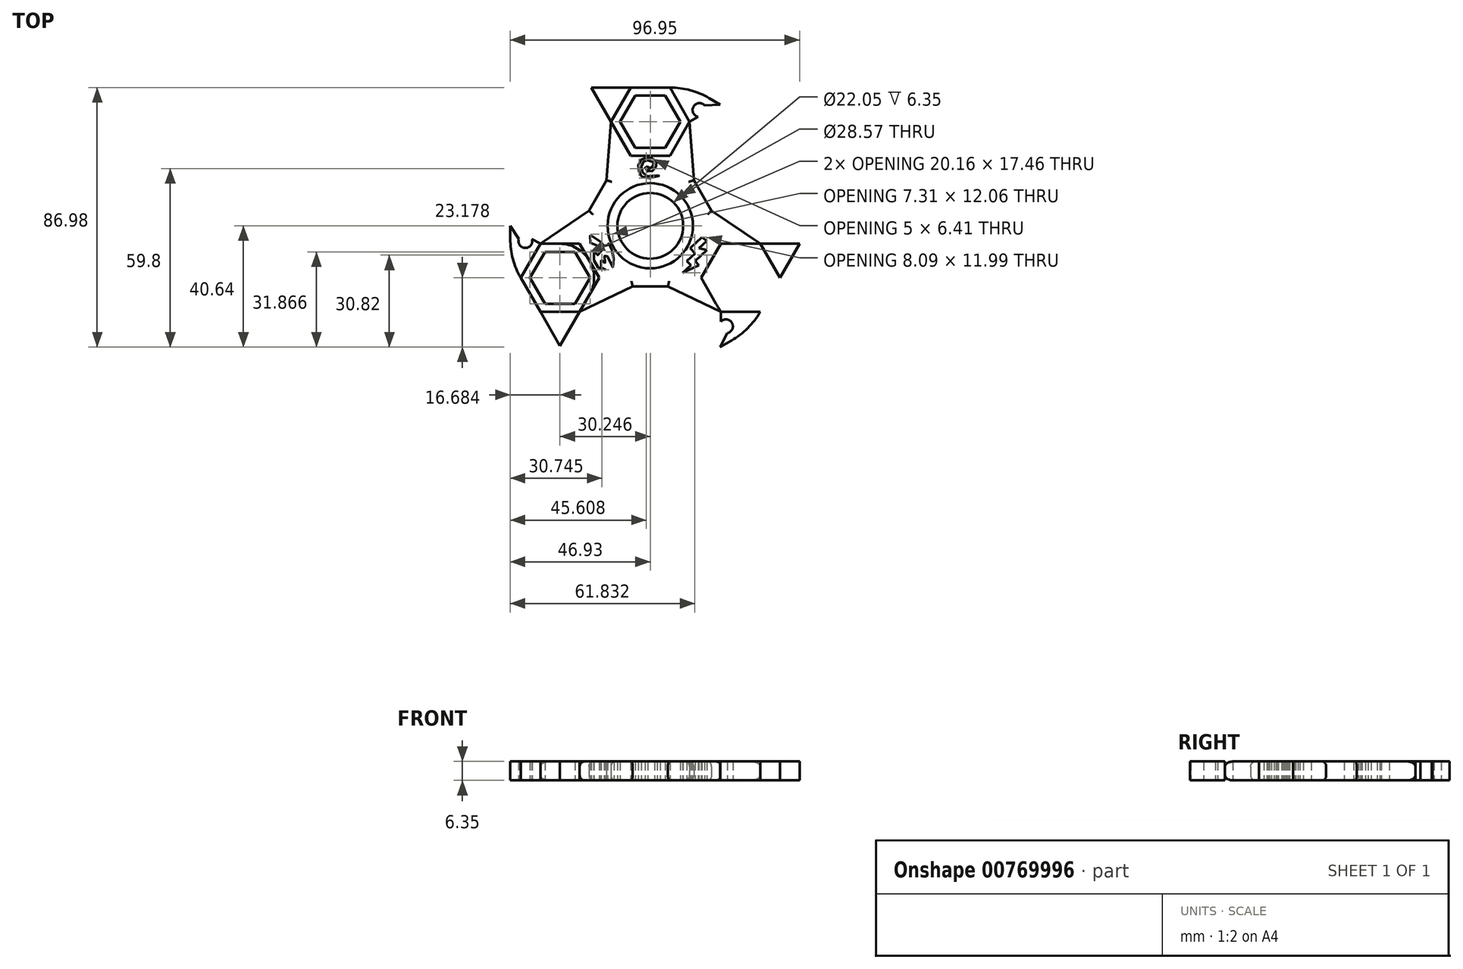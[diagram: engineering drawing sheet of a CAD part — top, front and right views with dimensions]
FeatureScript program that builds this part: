
annotation { "Feature Type Name" : "Feature", "Feature Type Description" : "" }
export const myFeature = defineFeature(function(context is Context, id is Id, definition is map)
    precondition{}
    {
        {
            var Q0;
            Q0=qCreatedBy(makeId("Top.planeOp"),FACE);
            var sketch = newSketch(context, id + "F0", { "sketchPlane" : qUnion([Q0])});
            skCircle(sketch, "E0", {"center": v(0, 0) * mm, "radius": 14.29 * mm});
            skCircle(sketch, "E1", {"center": v(0, 0) * mm, "radius": 11.02 * mm});
            skCircle(sketch, "E2.cCircle", {"center": v(0, 34.93) * mm, "radius": 8.73 * mm, "construction": true});
            skLineSegment(sketch, "E2.0", {"start": v(5.04, 26.2) * mm, "end": v(-5.04, 26.2) * mm});
            skLineSegment(sketch, "E2.1", {"start": v(-5.04, 26.2) * mm, "end": v(-10.08, 34.93) * mm});
            skLineSegment(sketch, "E2.2", {"start": v(-10.08, 34.92) * mm, "end": v(-5.04, 43.66) * mm});
            skLineSegment(sketch, "E2.3", {"start": v(-5.04, 43.66) * mm, "end": v(5.04, 43.66) * mm});
            skLineSegment(sketch, "E2.4", {"start": v(5.04, 43.66) * mm, "end": v(10.08, 34.92) * mm});
            skLineSegment(sketch, "E2.5", {"start": v(10.08, 34.93) * mm, "end": v(5.04, 26.2) * mm});
            skPoint(sketch, "E2.0.midPoint", {"position": v(0, 26.2) * mm});
            skCircle(sketch, "E3.cCircle", {"center": v(0, 34.93) * mm, "radius": 11.42 * mm, "construction": true});
            skLineSegment(sketch, "E3.0", {"start": v(6.6, 23.5) * mm, "end": v(-6.6, 23.5) * mm});
            skLineSegment(sketch, "E3.1", {"start": v(-6.6, 23.5) * mm, "end": v(-13.18, 34.93) * mm});
            skLineSegment(sketch, "E3.2", {"start": v(-13.18, 34.92) * mm, "end": v(-6.6, 46.34) * mm});
            skLineSegment(sketch, "E3.3", {"start": v(-6.6, 46.34) * mm, "end": v(6.6, 46.34) * mm});
            skLineSegment(sketch, "E3.4", {"start": v(6.6, 46.34) * mm, "end": v(13.18, 34.92) * mm});
            skLineSegment(sketch, "E3.5", {"start": v(13.18, 34.92) * mm, "end": v(6.6, 23.5) * mm});
            skPoint(sketch, "E3.0.midPoint", {"position": v(0, 23.5) * mm});
            skPoint(sketch, "E4.center", {"position": v(0.42, -0.28) * mm});
            skCircle(sketch, "E5.1.0", {"center": v(-30.25, -17.46) * mm, "radius": 11.42 * mm, "construction": true});
            skPoint(sketch, "E5.1.1", {"position": v(-20.36, -11.75) * mm});
            skPoint(sketch, "E5.1.2", {"position": v(-22.68, -13.1) * mm});
            skLineSegment(sketch, "E5.1.3", {"start": v(-23.65, -28.88) * mm, "end": v(-36.84, -28.88) * mm});
            skLineSegment(sketch, "E5.1.4", {"start": v(-17.06, -17.46) * mm, "end": v(-23.65, -28.88) * mm});
            skLineSegment(sketch, "E5.1.5", {"start": v(-36.84, -6.05) * mm, "end": v(-23.65, -6.05) * mm});
            skLineSegment(sketch, "E5.1.6", {"start": v(-43.43, -17.46) * mm, "end": v(-36.84, -6.05) * mm});
            skLineSegment(sketch, "E5.1.7", {"start": v(-35.29, -8.73) * mm, "end": v(-25.2, -8.73) * mm});
            skCircle(sketch, "E5.1.8", {"center": v(-30.25, -17.46) * mm, "radius": 8.73 * mm, "construction": true});
            skLineSegment(sketch, "E5.1.9", {"start": v(-40.33, -17.46) * mm, "end": v(-35.29, -8.73) * mm});
            skLineSegment(sketch, "E5.1.10", {"start": v(-20.16, -17.46) * mm, "end": v(-25.2, -26.2) * mm});
            skLineSegment(sketch, "E5.1.11", {"start": v(-35.29, -26.2) * mm, "end": v(-40.33, -17.46) * mm});
            skLineSegment(sketch, "E5.1.12", {"start": v(-25.2, -26.2) * mm, "end": v(-35.29, -26.2) * mm});
            skLineSegment(sketch, "E5.1.13", {"start": v(-36.84, -28.88) * mm, "end": v(-43.43, -17.46) * mm});
            skLineSegment(sketch, "E5.1.14", {"start": v(-23.65, -6.05) * mm, "end": v(-17.06, -17.46) * mm});
            skLineSegment(sketch, "E5.1.15", {"start": v(-25.2, -8.73) * mm, "end": v(-20.16, -17.46) * mm});
            skCircle(sketch, "E5.2.0", {"center": v(30.25, -17.46) * mm, "radius": 11.42 * mm, "construction": true});
            skPoint(sketch, "E5.2.1", {"position": v(20.36, -11.75) * mm});
            skPoint(sketch, "E5.2.2", {"position": v(22.68, -13.1) * mm});
            skLineSegment(sketch, "E5.2.3", {"start": v(36.84, -6.05) * mm, "end": v(43.43, -17.46) * mm});
            skLineSegment(sketch, "E5.2.4", {"start": v(23.65, -6.05) * mm, "end": v(36.84, -6.05) * mm});
            skLineSegment(sketch, "E5.2.5", {"start": v(23.65, -28.88) * mm, "end": v(17.06, -17.46) * mm});
            skLineSegment(sketch, "E5.2.6", {"start": v(36.84, -28.88) * mm, "end": v(23.65, -28.88) * mm});
            skLineSegment(sketch, "E5.2.7", {"start": v(25.2, -26.2) * mm, "end": v(20.16, -17.46) * mm});
            skCircle(sketch, "E5.2.8", {"center": v(30.25, -17.46) * mm, "radius": 8.73 * mm, "construction": true});
            skLineSegment(sketch, "E5.2.9", {"start": v(35.29, -26.2) * mm, "end": v(25.2, -26.2) * mm});
            skLineSegment(sketch, "E5.2.10", {"start": v(25.2, -8.73) * mm, "end": v(35.29, -8.73) * mm});
            skLineSegment(sketch, "E5.2.11", {"start": v(40.33, -17.46) * mm, "end": v(35.29, -26.2) * mm});
            skLineSegment(sketch, "E5.2.12", {"start": v(35.29, -8.73) * mm, "end": v(40.33, -17.46) * mm});
            skLineSegment(sketch, "E5.2.13", {"start": v(43.43, -17.46) * mm, "end": v(36.84, -28.88) * mm});
            skLineSegment(sketch, "E5.2.14", {"start": v(17.06, -17.46) * mm, "end": v(23.65, -6.05) * mm});
            skLineSegment(sketch, "E5.2.15", {"start": v(20.16, -17.46) * mm, "end": v(25.2, -8.73) * mm});
            skSolve(sketch);
        }
        {
            var Q0;
            Q0=qCreatedBy(makeId("Top.planeOp"),FACE);
            var sketch = newSketch(context, id + "F1", { "sketchPlane" : qUnion([Q0])});
            skLineSegment(sketch, "E6.0", {"start": v(-36.84, -6.05) * mm, "end": v(-23.65, -6.05) * mm});
            skCircle(sketch, "E6.1", {"center": v(0, 0) * mm, "radius": 14.29 * mm});
            skLineSegment(sketch, "E6.2", {"start": v(40.33, -17.46) * mm, "end": v(35.29, -26.2) * mm});
            skCircle(sketch, "E6.3", {"center": v(0, 0) * mm, "radius": 11.02 * mm});
            skCircle(sketch, "E6.4", {"center": v(-30.25, -17.46) * mm, "radius": 11.42 * mm});
            skLineSegment(sketch, "E6.5", {"start": v(-10.08, 34.92) * mm, "end": v(-5.04, 43.66) * mm});
            skLineSegment(sketch, "E6.6", {"start": v(-23.65, -28.88) * mm, "end": v(-36.84, -28.88) * mm});
            skLineSegment(sketch, "E6.7", {"start": v(23.65, -28.88) * mm, "end": v(17.06, -17.46) * mm});
            skCircle(sketch, "E6.8", {"center": v(30.25, -17.46) * mm, "radius": 8.73 * mm});
            skLineSegment(sketch, "E6.9", {"start": v(25.2, -26.2) * mm, "end": v(20.16, -17.46) * mm});
            skLineSegment(sketch, "E6.10", {"start": v(-6.6, 46.34) * mm, "end": v(6.6, 46.34) * mm});
            skLineSegment(sketch, "E6.11", {"start": v(-5.04, 26.2) * mm, "end": v(-10.08, 34.93) * mm});
            skLineSegment(sketch, "E6.12", {"start": v(35.29, -26.2) * mm, "end": v(25.2, -26.2) * mm});
            skCircle(sketch, "E6.13", {"center": v(30.25, -17.46) * mm, "radius": 11.42 * mm});
            skLineSegment(sketch, "E6.14", {"start": v(-5.04, 43.66) * mm, "end": v(5.04, 43.66) * mm});
            skLineSegment(sketch, "E6.15", {"start": v(5.04, 43.66) * mm, "end": v(10.08, 34.92) * mm});
            skLineSegment(sketch, "E6.16", {"start": v(-40.33, -17.46) * mm, "end": v(-35.29, -8.73) * mm});
            skLineSegment(sketch, "E6.17", {"start": v(-25.2, -26.2) * mm, "end": v(-35.29, -26.2) * mm});
            skLineSegment(sketch, "E6.18", {"start": v(10.08, 34.93) * mm, "end": v(5.04, 26.2) * mm});
            skLineSegment(sketch, "E6.19", {"start": v(43.43, -17.46) * mm, "end": v(36.84, -28.88) * mm});
            skCircle(sketch, "E6.20", {"center": v(0, 34.93) * mm, "radius": 11.42 * mm});
            skLineSegment(sketch, "E6.21", {"start": v(-35.29, -26.2) * mm, "end": v(-40.33, -17.46) * mm});
            skCircle(sketch, "E6.22", {"center": v(-30.25, -17.46) * mm, "radius": 8.73 * mm});
            skLineSegment(sketch, "E6.23", {"start": v(25.2, -8.73) * mm, "end": v(35.29, -8.73) * mm});
            skLineSegment(sketch, "E6.24", {"start": v(36.84, -6.05) * mm, "end": v(43.43, -17.46) * mm});
            skLineSegment(sketch, "E6.25", {"start": v(-17.06, -17.46) * mm, "end": v(-23.65, -28.88) * mm});
            skLineSegment(sketch, "E6.26", {"start": v(36.84, -28.88) * mm, "end": v(23.65, -28.88) * mm});
            skLineSegment(sketch, "E6.27", {"start": v(-35.29, -8.73) * mm, "end": v(-25.2, -8.73) * mm});
            skLineSegment(sketch, "E6.28", {"start": v(-36.84, -28.88) * mm, "end": v(-43.43, -17.46) * mm});
            skLineSegment(sketch, "E6.29", {"start": v(-13.18, 34.92) * mm, "end": v(-6.6, 46.34) * mm});
            skLineSegment(sketch, "E6.30", {"start": v(-6.6, 23.5) * mm, "end": v(-13.18, 34.93) * mm});
            skLineSegment(sketch, "E6.31", {"start": v(-20.16, -17.46) * mm, "end": v(-25.2, -26.2) * mm});
            skLineSegment(sketch, "E6.32", {"start": v(35.29, -8.73) * mm, "end": v(40.33, -17.46) * mm});
            skLineSegment(sketch, "E6.33", {"start": v(-43.43, -17.46) * mm, "end": v(-36.84, -6.05) * mm});
            skLineSegment(sketch, "E6.34", {"start": v(23.65, -6.05) * mm, "end": v(36.84, -6.05) * mm});
            skLineSegment(sketch, "E6.35", {"start": v(6.6, 46.34) * mm, "end": v(13.18, 34.92) * mm});
            skLineSegment(sketch, "E6.36", {"start": v(13.18, 34.92) * mm, "end": v(6.6, 23.5) * mm});
            skCircle(sketch, "E6.37", {"center": v(0, 34.93) * mm, "radius": 8.73 * mm});
            skLineSegment(sketch, "E6.38", {"start": v(20.16, -17.46) * mm, "end": v(25.2, -8.73) * mm});
            skLineSegment(sketch, "E6.39", {"start": v(6.6, 23.5) * mm, "end": v(-6.6, 23.5) * mm});
            skLineSegment(sketch, "E6.40", {"start": v(17.06, -17.46) * mm, "end": v(23.65, -6.05) * mm});
            skLineSegment(sketch, "E7", {"start": v(-14.64, 15.28) * mm, "end": v(-20.55, 5.04) * mm});
            skLineSegment(sketch, "E8", {"start": v(-36.84, -6.05) * mm, "end": v(-20.55, 5.04) * mm});
            skLineSegment(sketch, "E9", {"start": v(-14.64, 15.28) * mm, "end": v(-13.18, 34.92) * mm});
            skLineSegment(sketch, "E10.1.0", {"start": v(-5.91, -20.32) * mm, "end": v(-23.65, -28.88) * mm});
            skLineSegment(sketch, "E10.1.1", {"start": v(-5.91, -20.32) * mm, "end": v(5.91, -20.32) * mm});
            skLineSegment(sketch, "E10.1.2", {"start": v(23.65, -28.88) * mm, "end": v(5.91, -20.32) * mm});
            skLineSegment(sketch, "E10.2.0", {"start": v(20.55, 5.04) * mm, "end": v(36.84, -6.05) * mm});
            skLineSegment(sketch, "E10.2.1", {"start": v(20.55, 5.04) * mm, "end": v(14.64, 15.28) * mm});
            skLineSegment(sketch, "E10.2.2", {"start": v(13.18, 34.92) * mm, "end": v(14.64, 15.28) * mm});
            skArc(sketch, "E11", {"start": v(-46.93, -4.33) * mm, "mid": v(-46.05, -11.13) * mm, "end": v(-43.43, -17.46) * mm});
            skLineSegment(sketch, "E12", {"start": v(-46.93, -4.33) * mm, "end": v(-46.93, 0) * mm});
            skLineSegment(sketch, "E13", {"start": v(-36.84, -6.05) * mm, "end": v(-39.65, -4.42) * mm});
            skLineSegment(sketch, "E14", {"start": v(-46.93, 0) * mm, "end": v(-44.08, -4.4) * mm});
            skArc(sketch, "E15", {"start": v(-44.08, -4.4) * mm, "mid": v(-41.88, -7.44) * mm, "end": v(-39.65, -4.42) * mm});
            skArc(sketch, "E16.1.0", {"start": v(27.21, -38.48) * mm, "mid": v(32.66, -34.32) * mm, "end": v(36.84, -28.88) * mm});
            skLineSegment(sketch, "E16.1.1", {"start": v(23.46, -40.64) * mm, "end": v(25.85, -35.97) * mm});
            skLineSegment(sketch, "E16.1.2", {"start": v(27.21, -38.48) * mm, "end": v(23.46, -40.64) * mm});
            skArc(sketch, "E16.1.3", {"start": v(25.85, -35.97) * mm, "mid": v(27.38, -32.55) * mm, "end": v(23.65, -32.13) * mm});
            skLineSegment(sketch, "E16.1.4", {"start": v(23.65, -28.88) * mm, "end": v(23.65, -32.13) * mm});
            skArc(sketch, "E16.2.0", {"start": v(19.72, 42.8) * mm, "mid": v(13.39, 45.44) * mm, "end": v(6.6, 46.34) * mm});
            skLineSegment(sketch, "E16.2.1", {"start": v(23.46, 40.64) * mm, "end": v(18.23, 40.38) * mm});
            skLineSegment(sketch, "E16.2.2", {"start": v(19.72, 42.8) * mm, "end": v(23.46, 40.64) * mm});
            skArc(sketch, "E16.2.3", {"start": v(18.23, 40.38) * mm, "mid": v(14.5, 39.99) * mm, "end": v(16, 36.55) * mm});
            skLineSegment(sketch, "E16.2.4", {"start": v(13.18, 34.92) * mm, "end": v(16, 36.55) * mm});
            skPoint(sketch, "E17.endSnap0", {"position": v(-30.25, -28.88) * mm});
            skLineSegment(sketch, "E18", {"start": v(-30.25, -40.3) * mm, "end": v(-23.65, -28.88) * mm});
            skLineSegment(sketch, "E19", {"start": v(-36.84, -28.88) * mm, "end": v(-30.25, -40.3) * mm});
            skLineSegment(sketch, "E20.1.0", {"start": v(50.02, -6.05) * mm, "end": v(36.84, -6.05) * mm});
            skLineSegment(sketch, "E20.1.1", {"start": v(43.43, -17.46) * mm, "end": v(50.02, -6.05) * mm});
            skLineSegment(sketch, "E20.2.0", {"start": v(-19.78, 46.34) * mm, "end": v(-13.18, 34.92) * mm});
            skLineSegment(sketch, "E20.2.1", {"start": v(-6.6, 46.34) * mm, "end": v(-19.78, 46.34) * mm});
            skSolve(sketch);
        }
        {
            var Q0;
            Q0=makeQuery(id+"F1.imprint","IMPRINT",FACE,{"disambiguationData":[TD([[makeQuery(id+"F1.imprint","IMPRINT",EDGE,{"derivedFrom":sQuery(id+"F1.wireOp",EDGE,"E6.1")}),-1.0]])]});
            var Q1;
            Q1=makeQuery(id+"F0.imprint","IMPRINT",FACE,{"disambiguationData":[TD([[makeQuery(id+"F0.imprint","IMPRINT",EDGE,{"derivedFrom":sQuery(id+"F0.wireOp",EDGE,"E2.0")}),1.0]])]});
            var Q2;
            {var subQ0=sQuery(id+"F1.wireOp",EDGE,"E20.2.0");Q2=makeQuery(id+"F1.imprint","IMPRINT",FACE,{"disambiguationData":[TD([[makeQuery(id+"F1.imprint","IMPRINT",EDGE,{"derivedFrom":subQ0}),1.0]])]});}
            var Q3;
            {var subQ0=sQuery(id+"F1.wireOp",EDGE,"E16.2.0");Q3=makeQuery(id+"F1.imprint","IMPRINT",FACE,{"disambiguationData":[TD([[makeQuery(id+"F1.imprint","IMPRINT",EDGE,{"derivedFrom":subQ0}),1.0]])]});}
            var Q4;
            {var subQ0=sQuery(id+"F1.wireOp",EDGE,"E20.1.0");Q4=makeQuery(id+"F1.imprint","IMPRINT",FACE,{"disambiguationData":[TD([[makeQuery(id+"F1.imprint","IMPRINT",EDGE,{"derivedFrom":subQ0}),1.0]])]});}
            var Q5;
            Q5=makeQuery(id+"F0.imprint","IMPRINT",FACE,{"disambiguationData":[TD([[makeQuery(id+"F0.imprint","IMPRINT",EDGE,{"derivedFrom":sQuery(id+"F0.wireOp",EDGE,"E5.2.3")}),-1.0]])]});
            var Q6;
            {var subQ3=sQuery(id+"F1.wireOp",EDGE,"E16.1.0");Q6=makeQuery(id+"F1.imprint","IMPRINT",FACE,{"disambiguationData":[TD([[makeQuery(id+"F1.imprint","IMPRINT",EDGE,{"derivedFrom":subQ3}),1.0]])]});}
            var Q7;
            Q7=makeQuery(id+"F0.imprint","IMPRINT",FACE,{"disambiguationData":[TD([[makeQuery(id+"F0.imprint","IMPRINT",EDGE,{"derivedFrom":sQuery(id+"F0.wireOp",EDGE,"E5.1.3")}),-1.0]])]});
            var Q8;
            {var subQ0=sQuery(id+"F1.wireOp",EDGE,"E18");Q8=makeQuery(id+"F1.imprint","IMPRINT",FACE,{"disambiguationData":[TD([[makeQuery(id+"F1.imprint","IMPRINT",EDGE,{"derivedFrom":subQ0}),1.0]])]});}
            var Q9;
            {var subQ0=sQuery(id+"F1.wireOp",EDGE,"E11");Q9=makeQuery(id+"F1.imprint","IMPRINT",FACE,{"disambiguationData":[TD([[makeQuery(id+"F1.imprint","IMPRINT",EDGE,{"derivedFrom":subQ0}),1.0]])]});}
            var Q10;
            Q10=makeQuery(id+"F0.imprint","IMPRINT",FACE,{"disambiguationData":[TD([[makeQuery(id+"F0.imprint","IMPRINT",EDGE,{"derivedFrom":sQuery(id+"F0.wireOp",EDGE,"E0")}),1.0]])]});
            extrude(context, id + "F2", {"entities" : qUnion([Q0, Q1, Q2, Q3, Q4, Q5, Q6, Q7, Q8, Q9, Q10]), "depth" : 6.35 * mm, "offsetDistance" : 25.4 * mm});
        }
        {
            var Q0;
            Q0=qCreatedBy(makeId("Top.planeOp"),FACE);
            var sketch = newSketch(context, id + "F3", { "sketchPlane" : qUnion([Q0])});
            skLineSegment(sketch, "E21", {"start": v(16.34, -7.54) * mm, "end": v(18.95, -8.1) * mm});
            skLineSegment(sketch, "E22", {"start": v(18.95, -8.1) * mm, "end": v(14.98, -11.82) * mm});
            skLineSegment(sketch, "E23", {"start": v(14.98, -11.82) * mm, "end": v(16.34, -13.27) * mm});
            skLineSegment(sketch, "E24", {"start": v(16.34, -13.27) * mm, "end": v(10.86, -15.81) * mm});
            skLineSegment(sketch, "E25", {"start": v(10.86, -15.81) * mm, "end": v(13.6, -13.27) * mm});
            skPoint(sketch, "E25.endSnap0", {"position": v(13.6, -14.54) * mm});
            skLineSegment(sketch, "E26", {"start": v(13.6, -13.27) * mm, "end": v(12.25, -11.82) * mm});
            skLineSegment(sketch, "E27", {"start": v(12.25, -11.82) * mm, "end": v(14.98, -9.29) * mm});
            skLineSegment(sketch, "E28", {"start": v(14.98, -9.29) * mm, "end": v(13.36, -7.54) * mm});
            skLineSegment(sketch, "E29", {"start": v(13.36, -7.54) * mm, "end": v(17.37, -3.83) * mm});
            skPoint(sketch, "E30.endSnap0", {"position": v(15.37, -5.68) * mm});
            skLineSegment(sketch, "E31", {"start": v(16.34, -7.54) * mm, "end": v(18.95, -5.13) * mm});
            skLineSegment(sketch, "E32", {"start": v(18.95, -5.13) * mm, "end": v(17.37, -3.83) * mm});
            skFitSpline(sketch, "E33", {"points": [v(-0.88, 20.08) * mm, v(-1.58, 19.82) * mm, v(-1.58, 18.68) * mm, v(0, 18.16) * mm, v(1.3, 18.86) * mm, v(2.26, 21.13) * mm, v(1.21, 22.27) * mm, v(-0.8, 22.97) * mm, v(-3.15, 22.1) * mm, v(-4.03, 19.73) * mm, v(-3.42, 17.55) * mm, v(-1.58, 15.89) * mm, v(3.31, 17.02) * mm, v(-1.23, 16.68) * mm, v(-2.72, 18.42) * mm, v(-2.9, 20.26) * mm, v(-1.76, 22) * mm, v(0, 21.74) * mm, v(1.39, 20.87) * mm, v(0, 19.2) * mm, v(-0.8, 19.2) * mm, v(-0.88, 20.08) * mm]});
            skFitSpline(sketch, "E34", {"points": [v(-14.99, -14.8) * mm, v(-15.87, -14.46) * mm, v(-16.68, -13.5) * mm, v(-16.3, -11.53) * mm, v(-15.5, -12.4) * mm, v(-14.85, -11.66) * mm, v(-15.34, -9.75) * mm, v(-14.69, -9.82) * mm, v(-13.67, -11.37) * mm, v(-13.19, -12.66) * mm, v(-12.6, -13.9) * mm, v(-12.2, -11.2) * mm, v(-12.82, -8.21) * mm, v(-13.82, -6.12) * mm, v(-14.72, -5.63) * mm, v(-14.32, -7.02) * mm, v(-15.42, -6.93) * mm, v(-15.52, -5.93) * mm, v(-18.92, -4.35) * mm, v(-19.92, -2.66) * mm, v(-20.32, -4.15) * mm, v(-20, -5.85) * mm, v(-18.71, -6.34) * mm, v(-16.61, -7.83) * mm, v(-16.8, -9.82) * mm, v(-18.2, -9.33) * mm, v(-18.9, -8.54) * mm, v(-18.89, -11.53) * mm, v(-17.38, -14.12) * mm, v(-14.99, -14.8) * mm]});
            skLineSegment(sketch, "E35.0.0", {"start": v(23.65, -28.88) * mm, "end": v(36.84, -28.88) * mm});
            skLineSegment(sketch, "E35.0.1", {"start": v(36.84, -28.88) * mm, "end": v(43.43, -17.46) * mm});
            skLineSegment(sketch, "E35.0.2", {"start": v(43.43, -17.46) * mm, "end": v(36.84, -6.05) * mm});
            skLineSegment(sketch, "E35.0.3", {"start": v(36.84, -6.05) * mm, "end": v(23.65, -6.05) * mm});
            skLineSegment(sketch, "E35.0.4", {"start": v(23.65, -6.05) * mm, "end": v(17.06, -17.46) * mm});
            skLineSegment(sketch, "E35.0.5", {"start": v(17.06, -17.46) * mm, "end": v(23.65, -28.88) * mm});
            skSolve(sketch);
        }
        {
            var Q0;
            Q0 = qSketchRegion(id + "F3", true);
            extrude(context, id + "F4", {"entities" : qUnion([Q0]), "operationType" : NewBodyOperationType.REMOVE, "depth" : 6.35 * mm, "offsetDistance" : 25.4 * mm});
        }
        {
            var Q0;
            Q0=makeQuery(id+"F2.opExtrude","CAP_EDGE",EDGE,{"disambiguationData":[OSD([sQuery(id+"F1.wireOp",EDGE,"E10.2.2")])],"isStart":false});
            var Q1;
            Q1=makeQuery(id+"F2.opExtrude","CAP_EDGE",EDGE,{"disambiguationData":[OSD([sQuery(id+"F1.wireOp",EDGE,"E10.2.1")])],"isStart":false});
            var Q2;
            Q2=makeQuery(id+"F2.opExtrude","CAP_EDGE",EDGE,{"disambiguationData":[OSD([sQuery(id+"F1.wireOp",EDGE,"E10.2.0")])],"isStart":false});
            var Q3;
            Q3=makeQuery(id+"F2.opExtrude","CAP_EDGE",EDGE,{"disambiguationData":[OSD([sQuery(id+"F1.wireOp",EDGE,"E10.2.2")])],"isStart":true});
            var Q4;
            Q4=makeQuery(id+"F2.opExtrude","CAP_EDGE",EDGE,{"disambiguationData":[OSD([sQuery(id+"F1.wireOp",EDGE,"E10.2.1")])],"isStart":true});
            var Q5;
            Q5=makeQuery(id+"F2.opExtrude","CAP_EDGE",EDGE,{"disambiguationData":[OSD([sQuery(id+"F1.wireOp",EDGE,"E10.2.0")])],"isStart":true});
            var Q6;
            Q6=makeQuery(id+"F2.opExtrude","CAP_EDGE",EDGE,{"disambiguationData":[OSD([sQuery(id+"F1.wireOp",EDGE,"E9")])],"isStart":false});
            var Q7;
            Q7=makeQuery(id+"F2.opExtrude","CAP_EDGE",EDGE,{"disambiguationData":[OSD([sQuery(id+"F1.wireOp",EDGE,"E7")])],"isStart":false});
            var Q8;
            Q8=makeQuery(id+"F2.opExtrude","CAP_EDGE",EDGE,{"disambiguationData":[OSD([sQuery(id+"F1.wireOp",EDGE,"E8")])],"isStart":false});
            var Q9;
            Q9=makeQuery(id+"F2.opExtrude","CAP_EDGE",EDGE,{"disambiguationData":[OSD([sQuery(id+"F1.wireOp",EDGE,"E7")])],"isStart":true});
            var Q10;
            Q10=makeQuery(id+"F2.opExtrude","CAP_EDGE",EDGE,{"disambiguationData":[OSD([sQuery(id+"F1.wireOp",EDGE,"E9")])],"isStart":true});
            var Q11;
            Q11=makeQuery(id+"F2.opExtrude","CAP_EDGE",EDGE,{"disambiguationData":[OSD([sQuery(id+"F1.wireOp",EDGE,"E8")])],"isStart":true});
            var Q12;
            Q12=makeQuery(id+"F2.opExtrude","CAP_EDGE",EDGE,{"disambiguationData":[OSD([sQuery(id+"F1.wireOp",EDGE,"E10.1.1")])],"isStart":true});
            var Q13;
            Q13=makeQuery(id+"F2.opExtrude","CAP_EDGE",EDGE,{"disambiguationData":[OSD([sQuery(id+"F1.wireOp",EDGE,"E10.1.0")])],"isStart":false});
            var Q14;
            Q14=makeQuery(id+"F2.opExtrude","CAP_EDGE",EDGE,{"disambiguationData":[OSD([sQuery(id+"F1.wireOp",EDGE,"E10.1.0")])],"isStart":true});
            var Q15;
            Q15=makeQuery(id+"F2.opExtrude","CAP_EDGE",EDGE,{"disambiguationData":[OSD([sQuery(id+"F1.wireOp",EDGE,"E10.1.1")])],"isStart":false});
            var Q16;
            Q16=makeQuery(id+"F2.opExtrude","CAP_EDGE",EDGE,{"disambiguationData":[OSD([sQuery(id+"F1.wireOp",EDGE,"E10.1.2")])],"isStart":false});
            var Q17;
            Q17=makeQuery(id+"F2.opExtrude","CAP_EDGE",EDGE,{"disambiguationData":[OSD([sQuery(id+"F1.wireOp",EDGE,"E10.1.2")])],"isStart":true});
            fillet(context, id + "F5", {"entities" : qUnion([Q0, Q1, Q2, Q3, Q4, Q5, Q6, Q7, Q8, Q9, Q10, Q11, Q12, Q13, Q14, Q15, Q16, Q17]), "radius" : 1.78 * mm, "tangentPropagation" : true, "allowEdgeOverflow" : false});
        }
    });
